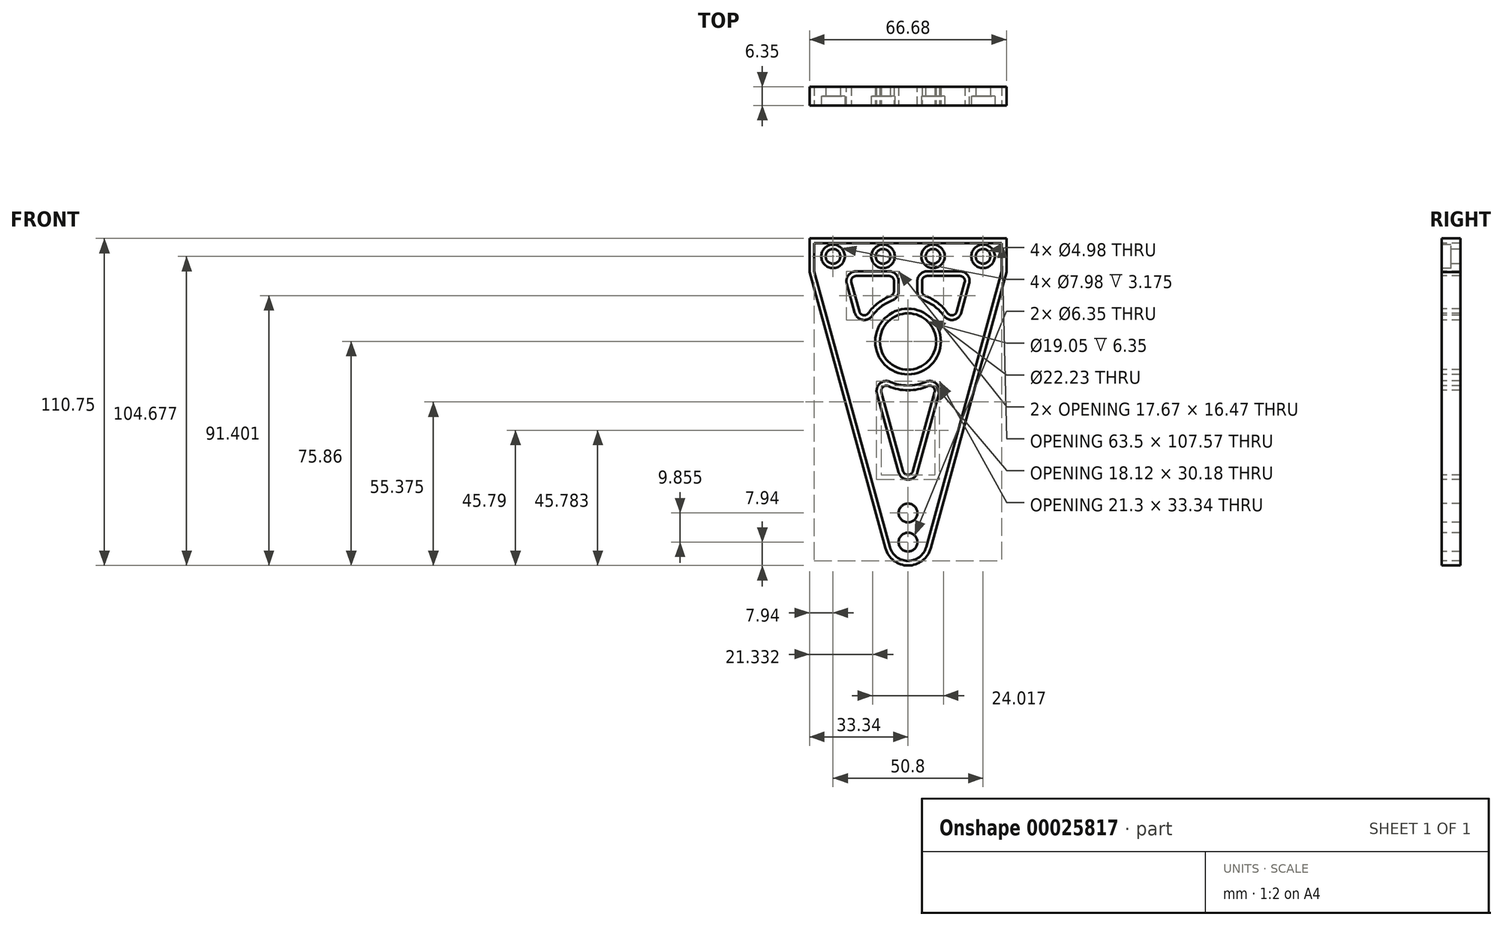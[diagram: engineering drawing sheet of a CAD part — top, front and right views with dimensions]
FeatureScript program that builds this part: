
annotation { "Feature Type Name" : "Feature", "Feature Type Description" : "" }
export const myFeature = defineFeature(function(context is Context, id is Id, definition is map)
    precondition{}
    {
        {
            var Q0;
            Q0=qCreatedBy(makeId("Front.planeOp"),FACE);
            var sketch = newSketch(context, id + "F0", { "sketchPlane" : qUnion([Q0])});
            skCircle(sketch, "E0", {"center": v(0, 0) * mm, "radius": 11.11 * mm});
            skLineSegment(sketch, "E1", {"start": v(0, 0) * mm, "end": v(0, 33.3) * mm, "construction": true});
            skLineSegment(sketch, "E2", {"start": v(0, 0) * mm, "end": v(25.23, 0) * mm, "construction": true});
            skLineSegment(sketch, "E3", {"start": v(-31.75, 33.3) * mm, "end": v(31.75, 33.3) * mm});
            skLineSegment(sketch, "E4", {"start": v(31.75, 33.3) * mm, "end": v(31.75, 23.77) * mm});
            skLineSegment(sketch, "E5", {"start": v(31.75, 23.77) * mm, "end": v(6.12, -69.6) * mm});
            skLineSegment(sketch, "E6", {"start": v(-6.12, -69.6) * mm, "end": v(-31.75, 23.77) * mm});
            skLineSegment(sketch, "E7", {"start": v(-31.75, 23.77) * mm, "end": v(-31.75, 33.3) * mm});
            skArc(sketch, "E8", {"start": v(-6.12, -69.6) * mm, "mid": v(0, -74.27) * mm, "end": v(6.12, -69.6) * mm});
            skSolve(sketch);
        }
        {
            var Q0;
            Q0=makeQuery(id+"F0.imprint","IMPRINT",FACE,{"disambiguationData":[TD([[makeQuery(id+"F0.imprint","IMPRINT",EDGE,{"derivedFrom":sQuery(id+"F0.wireOp",EDGE,"E0")}),-1.0]])]});
            extrude(context, id + "F1", {"entities" : qUnion([Q0]), "depth" : 6.35 * mm});
        }
        {
            var Q0;
            Q0=makeQuery(id+"F1.opExtrude","CAP_FACE",FACE,{"disambiguationData":[OSD([sQuery(id+"F0.wireOp",EDGE,"E0"),sQuery(id+"F0.wireOp",EDGE,"E3"),sQuery(id+"F0.wireOp",EDGE,"E4"),sQuery(id+"F0.wireOp",EDGE,"E5"),sQuery(id+"F0.wireOp",EDGE,"E6"),sQuery(id+"F0.wireOp",EDGE,"E7"),sQuery(id+"F0.wireOp",EDGE,"E8")])],"isStart":false});
            var sketch = newSketch(context, id + "F2", { "sketchPlane" : qUnion([Q0])});
            skLineSegment(sketch, "E9.0", {"start": v(21.87, 23.77) * mm, "end": v(3.17, 23.77) * mm});
            skLineSegment(sketch, "E9.2", {"start": v(0, -55.92) * mm, "end": v(13.77, -5.75) * mm});
            skLineSegment(sketch, "E9.3", {"start": v(-21.87, 23.77) * mm, "end": v(-14.78, -2.08) * mm});
            skArc(sketch, "E10", {"start": v(-13.77, -5.75) * mm, "mid": v(0, -14.92) * mm, "end": v(13.77, -5.75) * mm});
            skLineSegment(sketch, "E11.trimOffspring", {"start": v(-13.77, -5.75) * mm, "end": v(0, -55.92) * mm});
            skArc(sketch, "E12.trimOffspring", {"start": v(14.78, -2.08) * mm, "mid": v(12.25, 8.53) * mm, "end": v(3.18, 14.58) * mm});
            skLineSegment(sketch, "E13.trimOffspring", {"start": v(14.78, -2.08) * mm, "end": v(21.87, 23.77) * mm});
            skLineSegment(sketch, "E14", {"start": v(0, 0) * mm, "end": v(0, 33.3) * mm, "construction": true});
            skLineSegment(sketch, "E15.left", {"start": v(3.18, 14.58) * mm, "end": v(3.17, 23.77) * mm});
            skLineSegment(sketch, "E15.right", {"start": v(-3.18, 14.58) * mm, "end": v(-3.17, 23.77) * mm});
            skArc(sketch, "E16.trimOffspring", {"start": v(-3.18, 14.58) * mm, "mid": v(-12.25, 8.53) * mm, "end": v(-14.78, -2.08) * mm});
            skLineSegment(sketch, "E17.trimOffspring", {"start": v(-3.18, 23.77) * mm, "end": v(-21.87, 23.77) * mm});
            skSolve(sketch);
        }
        {
            var Q0;
            Q0=makeQuery(id+"F2.imprint","IMPRINT",FACE,{"disambiguationData":[TD([[makeQuery(id+"F2.imprint","IMPRINT",EDGE,{"derivedFrom":sQuery(id+"F2.wireOp",EDGE,"E9.0")}),1.0]])]});
            var Q1;
            Q1=makeQuery(id+"F2.imprint","IMPRINT",FACE,{"disambiguationData":[TD([[makeQuery(id+"F2.imprint","IMPRINT",EDGE,{"derivedFrom":sQuery(id+"F2.wireOp",EDGE,"E9.3")}),1.0]])]});
            var Q2;
            Q2=makeQuery(id+"F2.imprint","IMPRINT",FACE,{"disambiguationData":[TD([[makeQuery(id+"F2.imprint","IMPRINT",EDGE,{"derivedFrom":sQuery(id+"F2.wireOp",EDGE,"E9.2")}),1.0]])]});
            extrude(context, id + "F3", {"entities" : qUnion([Q0, Q1, Q2]), "operationType" : NewBodyOperationType.REMOVE, "endBound" : BoundingType.THROUGH_ALL, "oppositeDirection" : true, "depth" : 25.4 * mm});
        }
        {
            var Q0;
            Q0=makeQuery(id+"F3.boolean.opBoolean","COPY",EDGE,{"derivedFrom":makeQuery(id+"F3.opExtrude","SWEPT_EDGE",EDGE,{"disambiguationData":[OSD([sQuery(id+"F2.wireOp",EDGE,"E9.3"),sQuery(id+"F2.wireOp",EDGE,"E17.trimOffspring")])]})});
            var Q1;
            Q1=makeQuery(id+"F3.boolean.opBoolean","COPY",EDGE,{"derivedFrom":makeQuery(id+"F3.opExtrude","SWEPT_EDGE",EDGE,{"disambiguationData":[OSD([sQuery(id+"F2.wireOp",EDGE,"E15.right"),sQuery(id+"F2.wireOp",EDGE,"E16.trimOffspring")])]})});
            var Q2;
            Q2=makeQuery(id+"F3.boolean.opBoolean","COPY",EDGE,{"derivedFrom":makeQuery(id+"F3.opExtrude","SWEPT_EDGE",EDGE,{"disambiguationData":[OSD([sQuery(id+"F2.wireOp",EDGE,"E9.3"),sQuery(id+"F2.wireOp",EDGE,"E16.trimOffspring")])]})});
            var Q3;
            Q3=makeQuery(id+"F3.boolean.opBoolean","COPY",EDGE,{"derivedFrom":makeQuery(id+"F3.opExtrude","SWEPT_EDGE",EDGE,{"disambiguationData":[OSD([sQuery(id+"F2.wireOp",EDGE,"E9.0"),sQuery(id+"F2.wireOp",EDGE,"E13.trimOffspring")])]})});
            var Q4;
            Q4=makeQuery(id+"F3.boolean.opBoolean","COPY",EDGE,{"derivedFrom":makeQuery(id+"F3.opExtrude","SWEPT_EDGE",EDGE,{"disambiguationData":[OSD([sQuery(id+"F2.wireOp",EDGE,"E9.0"),sQuery(id+"F2.wireOp",EDGE,"E15.left")])]})});
            var Q5;
            Q5=makeQuery(id+"F3.boolean.opBoolean","COPY",EDGE,{"derivedFrom":makeQuery(id+"F3.opExtrude","SWEPT_EDGE",EDGE,{"disambiguationData":[OSD([sQuery(id+"F2.wireOp",EDGE,"E12.trimOffspring"),sQuery(id+"F2.wireOp",EDGE,"E13.trimOffspring")])]})});
            var Q6;
            Q6=makeQuery(id+"F3.boolean.opBoolean","COPY",EDGE,{"derivedFrom":makeQuery(id+"F3.opExtrude","SWEPT_EDGE",EDGE,{"disambiguationData":[OSD([sQuery(id+"F2.wireOp",EDGE,"E9.2"),sQuery(id+"F2.wireOp",EDGE,"E10")])]})});
            var Q7;
            Q7=makeQuery(id+"F3.boolean.opBoolean","COPY",EDGE,{"derivedFrom":makeQuery(id+"F3.opExtrude","SWEPT_EDGE",EDGE,{"disambiguationData":[OSD([sQuery(id+"F2.wireOp",EDGE,"E10"),sQuery(id+"F2.wireOp",EDGE,"E11.trimOffspring")])]})});
            var Q8;
            Q8=makeQuery(id+"F3.boolean.opBoolean","COPY",EDGE,{"derivedFrom":makeQuery(id+"F3.opExtrude","SWEPT_EDGE",EDGE,{"disambiguationData":[OSD([sQuery(id+"F2.wireOp",EDGE,"E9.2"),sQuery(id+"F2.wireOp",EDGE,"E11.trimOffspring")])]})});
            var Q9;
            Q9=makeQuery(id+"F3.boolean.opBoolean","COPY",EDGE,{"derivedFrom":makeQuery(id+"F3.opExtrude","SWEPT_EDGE",EDGE,{"disambiguationData":[OSD([sQuery(id+"F2.wireOp",EDGE,"E15.right"),sQuery(id+"F2.wireOp",EDGE,"E17.trimOffspring")])]})});
            var Q10;
            Q10=makeQuery(id+"F3.boolean.opBoolean","COPY",EDGE,{"derivedFrom":makeQuery(id+"F3.opExtrude","SWEPT_EDGE",EDGE,{"disambiguationData":[OSD([sQuery(id+"F2.wireOp",EDGE,"E12.trimOffspring"),sQuery(id+"F2.wireOp",EDGE,"E15.left")])]})});
            fillet(context, id + "F4", {"entities" : qUnion([Q0, Q1, Q2, Q3, Q4, Q5, Q6, Q7, Q8, Q9, Q10]), "radius" : 3.3 * mm, "tangentPropagation" : true, "allowEdgeOverflow" : false});
        }
        {
            var Q0;
            Q0=makeQuery(id+"F1.opExtrude","CAP_FACE",FACE,{"disambiguationData":[OSD([sQuery(id+"F0.wireOp",EDGE,"E0"),sQuery(id+"F0.wireOp",EDGE,"E3"),sQuery(id+"F0.wireOp",EDGE,"E4"),sQuery(id+"F0.wireOp",EDGE,"E5"),sQuery(id+"F0.wireOp",EDGE,"E6"),sQuery(id+"F0.wireOp",EDGE,"E7"),sQuery(id+"F0.wireOp",EDGE,"E8")])],"isStart":false});
            var sketch = newSketch(context, id + "F5", { "sketchPlane" : qUnion([Q0])});
            skCircle(sketch, "E18", {"center": v(0, -58.06) * mm, "radius": 3.18 * mm});
            skCircle(sketch, "E19", {"center": v(0, -67.92) * mm, "radius": 3.18 * mm});
            skLineSegment(sketch, "E20", {"start": v(-25.4, 28.82) * mm, "end": v(25.4, 28.82) * mm});
            skPoint(sketch, "E21", {"position": v(-8.46, 28.82) * mm});
            skPoint(sketch, "E22", {"position": v(8.46, 28.82) * mm});
            skLineSegment(sketch, "E23", {"start": v(0, 0) * mm, "end": v(0, 33.3) * mm, "construction": true});
            skSolve(sketch);
        }
        {
            var Q0;
            Q0=sQuery(id+"F5.wireOp",VERTEX,"E18.center");
            var Q1;
            Q1=sQuery(id+"F5.wireOp",VERTEX,"E19.center");
            var Q2;
            Q2=makeQuery(id+"F1.opExtrude","SWEPT_BODY",BODY,{"disambiguationData":[OSD([sQuery(id+"F0.wireOp",EDGE,"E0"),sQuery(id+"F0.wireOp",EDGE,"E3"),sQuery(id+"F0.wireOp",EDGE,"E4"),sQuery(id+"F0.wireOp",EDGE,"E5"),sQuery(id+"F0.wireOp",EDGE,"E6"),sQuery(id+"F0.wireOp",EDGE,"E7"),sQuery(id+"F0.wireOp",EDGE,"E8")])]});
            hole(context, id + "F6", {"style" : HoleStyle.SIMPLE, "holeDiameter" : 6.35 * mm, "endStyle" : HoleEndStyle.THROUGH, "locations" : qUnion([Q0, Q1]), "scope" : qUnion([Q2])});
        }
        {
            var Q0;
            Q0=sQuery(id+"F5.wireOp",VERTEX,"E20.start");
            var Q1;
            Q1=sQuery(id+"F5.wireOp",VERTEX,"E21");
            var Q2;
            Q2=sQuery(id+"F5.wireOp",VERTEX,"E22");
            var Q3;
            Q3=sQuery(id+"F5.wireOp",VERTEX,"E20.end");
            var Q4;
            Q4=makeQuery(id+"F1.opExtrude","SWEPT_BODY",BODY,{"disambiguationData":[OSD([sQuery(id+"F0.wireOp",EDGE,"E0"),sQuery(id+"F0.wireOp",EDGE,"E3"),sQuery(id+"F0.wireOp",EDGE,"E4"),sQuery(id+"F0.wireOp",EDGE,"E5"),sQuery(id+"F0.wireOp",EDGE,"E6"),sQuery(id+"F0.wireOp",EDGE,"E7"),sQuery(id+"F0.wireOp",EDGE,"E8")])]});
            hole(context, id + "F7", {"style" : HoleStyle.C_BORE, "holeDiameter" : 4.98 * mm, "cBoreDiameter" : 7.98 * mm, "cBoreDepth" : 3.17 * mm, "endStyle" : HoleEndStyle.THROUGH, "locations" : qUnion([Q0, Q1, Q2, Q3]), "scope" : qUnion([Q4])});
        }
        {
            var Q0;
            Q0=makeQuery(id+"F1.opExtrude","CAP_FACE",FACE,{"disambiguationData":[OSD([sQuery(id+"F0.wireOp",EDGE,"E0"),sQuery(id+"F0.wireOp",EDGE,"E3"),sQuery(id+"F0.wireOp",EDGE,"E4"),sQuery(id+"F0.wireOp",EDGE,"E5"),sQuery(id+"F0.wireOp",EDGE,"E6"),sQuery(id+"F0.wireOp",EDGE,"E7"),sQuery(id+"F0.wireOp",EDGE,"E8")])],"isStart":false});
            var sketch = newSketch(context, id + "F8", { "sketchPlane" : qUnion([Q0])});
            skLineSegment(sketch, "E24.0", {"start": v(-7.65, -70.02) * mm, "end": v(-33.34, 23.56) * mm});
            skArc(sketch, "E24.1", {"start": v(-7.65, -70.02) * mm, "mid": v(0, -75.86) * mm, "end": v(7.65, -70.02) * mm});
            skLineSegment(sketch, "E24.2", {"start": v(33.34, 23.56) * mm, "end": v(7.65, -70.02) * mm});
            skLineSegment(sketch, "E24.3", {"start": v(33.34, 34.89) * mm, "end": v(33.34, 23.56) * mm});
            skLineSegment(sketch, "E24.4", {"start": v(-33.34, 34.89) * mm, "end": v(33.34, 34.89) * mm});
            skLineSegment(sketch, "E24.5", {"start": v(-33.34, 23.56) * mm, "end": v(-33.34, 34.89) * mm});
            skArc(sketch, "E25.0", {"start": v(-6.48, 22.19) * mm, "mid": v(-5.26, 21.68) * mm, "end": v(-4.76, 20.47) * mm});
            skLineSegment(sketch, "E25.1", {"start": v(-4.76, 17.03) * mm, "end": v(-4.76, 20.47) * mm});
            skArc(sketch, "E25.2", {"start": v(-4.76, 17.03) * mm, "mid": v(-5.07, 16.06) * mm, "end": v(-5.87, 15.43) * mm});
            skArc(sketch, "E25.3", {"start": v(-5.87, 15.43) * mm, "mid": v(-10.08, 13.07) * mm, "end": v(-13.44, 9.6) * mm});
            skArc(sketch, "E25.4", {"start": v(-13.44, 9.6) * mm, "mid": v(-15.13, 8.9) * mm, "end": v(-16.48, 10.14) * mm});
            skLineSegment(sketch, "E25.5", {"start": v(-6.48, 22.19) * mm, "end": v(-17.54, 22.19) * mm});
            skLineSegment(sketch, "E25.6", {"start": v(-19.2, 20.02) * mm, "end": v(-16.48, 10.14) * mm});
            skArc(sketch, "E25.7", {"start": v(-19.2, 20.02) * mm, "mid": v(-18.9, 21.51) * mm, "end": v(-17.54, 22.19) * mm});
            skArc(sketch, "E26.0", {"start": v(17.54, 22.19) * mm, "mid": v(18.9, 21.51) * mm, "end": v(19.2, 20.02) * mm});
            skLineSegment(sketch, "E26.1", {"start": v(16.48, 10.14) * mm, "end": v(19.2, 20.02) * mm});
            skArc(sketch, "E26.2", {"start": v(16.48, 10.14) * mm, "mid": v(15.13, 8.9) * mm, "end": v(13.44, 9.6) * mm});
            skArc(sketch, "E26.3", {"start": v(13.44, 9.6) * mm, "mid": v(10.08, 13.07) * mm, "end": v(5.87, 15.43) * mm});
            skArc(sketch, "E26.4", {"start": v(5.87, 15.43) * mm, "mid": v(5.07, 16.06) * mm, "end": v(4.76, 17.03) * mm});
            skLineSegment(sketch, "E26.5", {"start": v(17.54, 22.19) * mm, "end": v(6.48, 22.19) * mm});
            skLineSegment(sketch, "E26.6", {"start": v(4.76, 17.03) * mm, "end": v(4.76, 20.47) * mm});
            skArc(sketch, "E26.7", {"start": v(4.76, 20.47) * mm, "mid": v(5.26, 21.68) * mm, "end": v(6.48, 22.19) * mm});
            skCircle(sketch, "E27.0", {"center": v(0, 0) * mm, "radius": 9.53 * mm});
            skArc(sketch, "E28.0", {"start": v(-6.66, -15.1) * mm, "mid": v(0, -16.5) * mm, "end": v(6.66, -15.1) * mm});
            skArc(sketch, "E28.1", {"start": v(-9, -17.13) * mm, "mid": v(-8.47, -15.38) * mm, "end": v(-6.66, -15.1) * mm});
            skLineSegment(sketch, "E28.2", {"start": v(-9, -17.13) * mm, "end": v(-1.65, -43.9) * mm});
            skArc(sketch, "E28.3", {"start": v(1.65, -43.9) * mm, "mid": v(0, -45.16) * mm, "end": v(-1.65, -43.9) * mm});
            skLineSegment(sketch, "E28.4", {"start": v(1.65, -43.9) * mm, "end": v(9, -17.13) * mm});
            skArc(sketch, "E28.5", {"start": v(6.66, -15.1) * mm, "mid": v(8.47, -15.38) * mm, "end": v(9, -17.13) * mm});
            skSolve(sketch);
        }
        {
            var Q0;
            Q0=makeQuery(id+"F8.imprint","IMPRINT",FACE,{"disambiguationData":[TD([[makeQuery(id+"F8.imprint","IMPRINT",EDGE,{"derivedFrom":sQuery(id+"F8.wireOp",EDGE,"E25.0")}),1.0]])]});
            var Q1;
            Q1=makeQuery(id+"F8.imprint","IMPRINT",FACE,{"disambiguationData":[TD([[makeQuery(id+"F8.imprint","IMPRINT",EDGE,{"derivedFrom":sQuery(id+"F8.wireOp",EDGE,"E26.0")}),1.0]])]});
            var Q2;
            Q2=makeQuery(id+"F8.imprint","IMPRINT",FACE,{"disambiguationData":[TD([[makeQuery(id+"F8.imprint","IMPRINT",EDGE,{"derivedFrom":sQuery(id+"F8.wireOp",EDGE,"E27.0")}),-1.0]])]});
            var Q3;
            Q3=makeQuery(id+"F8.imprint","IMPRINT",FACE,{"disambiguationData":[TD([[makeQuery(id+"F8.imprint","IMPRINT",EDGE,{"derivedFrom":sQuery(id+"F8.wireOp",EDGE,"E28.0")}),1.0]])]});
            var Q4;
            Q4=makeQuery(id+"F8.imprint","IMPRINT",FACE,{"disambiguationData":[TD([[makeQuery(id+"F8.imprint","IMPRINT",EDGE,{"derivedFrom":sQuery(id+"F8.wireOp",EDGE,"E24.0")}),-1.0]])]});
            extrude(context, id + "F9", {"entities" : qUnion([Q0, Q1, Q2, Q3, Q4]), "oppositeDirection" : true, "depth" : 6.35 * mm});
        }
    });
